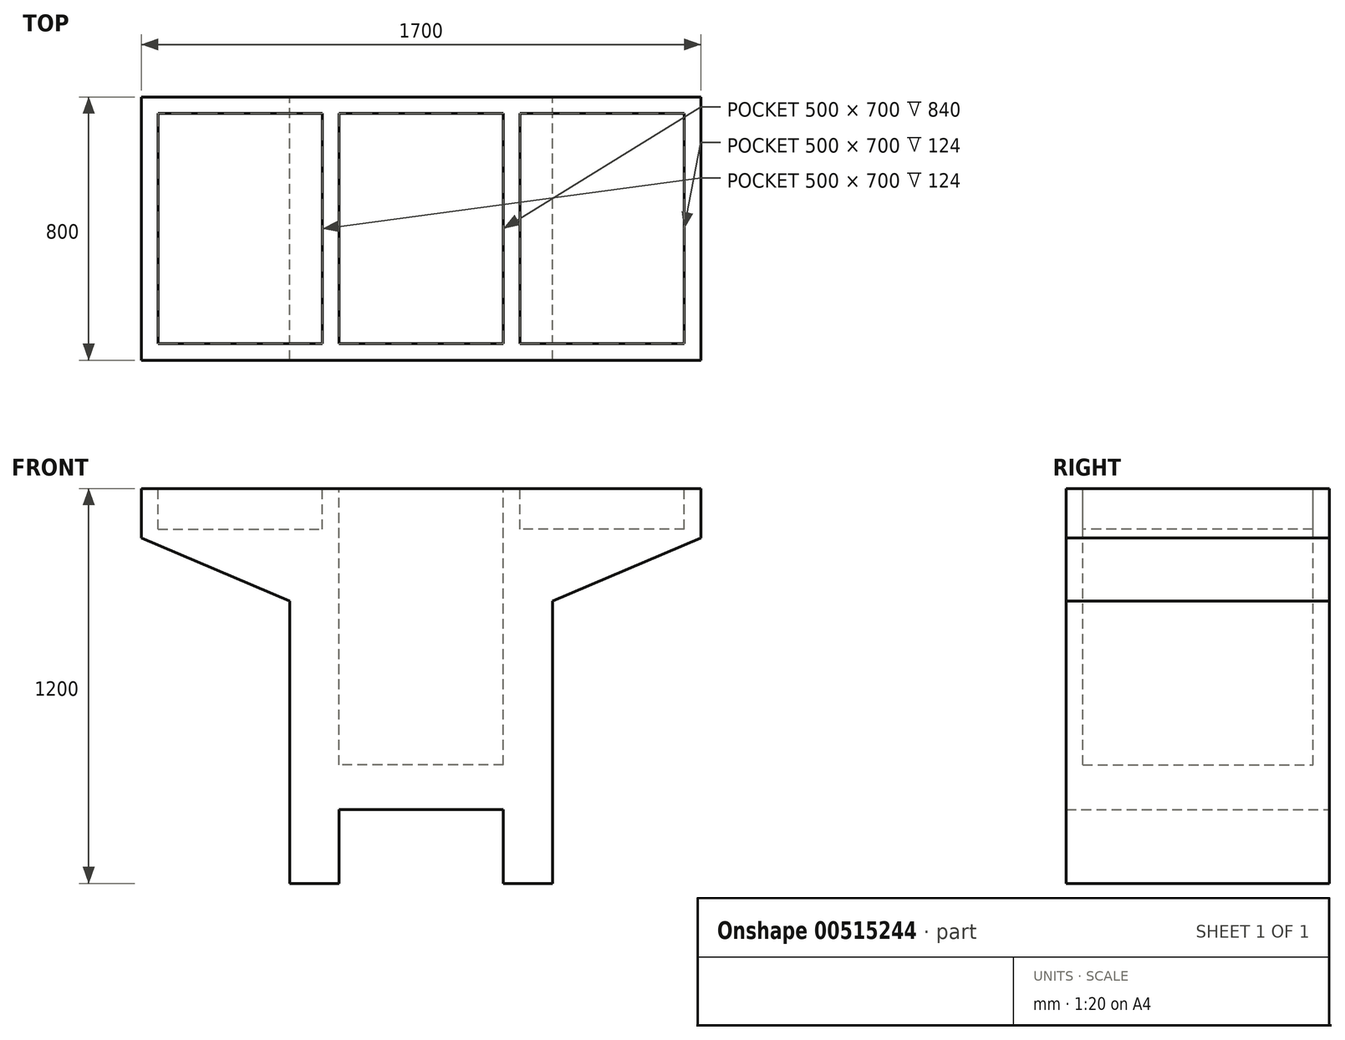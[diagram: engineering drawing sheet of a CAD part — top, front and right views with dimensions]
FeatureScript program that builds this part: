
annotation { "Feature Type Name" : "Feature", "Feature Type Description" : "" }
export const myFeature = defineFeature(function(context is Context, id is Id, definition is map)
    precondition{}
    {
        {
            var Q0;
            Q0=qCreatedBy(makeId("Front.planeOp"),FACE);
            var sketch = newSketch(context, id + "F0", { "sketchPlane" : qUnion([Q0])});
            skLineSegment(sketch, "E0", {"start": v(0, 224.9) * mm, "end": v(-250, 224.9) * mm});
            skLineSegment(sketch, "E1", {"start": v(-250, 224.9) * mm, "end": v(-250, 0) * mm});
            skLineSegment(sketch, "E2", {"start": v(-250, 0) * mm, "end": v(-400, 0) * mm});
            skLineSegment(sketch, "E3", {"start": v(-400, 0) * mm, "end": v(-400, 858.13) * mm});
            skLineSegment(sketch, "E4", {"start": v(-400, 858.13) * mm, "end": v(-850, 1050) * mm});
            skLineSegment(sketch, "E5", {"start": v(-850, 1050) * mm, "end": v(-850, 1200) * mm});
            skLineSegment(sketch, "E6", {"start": v(-850, 1200) * mm, "end": v(0, 1200) * mm});
            skLineSegment(sketch, "E7.MirrorCS", {"start": v(850, 1200) * mm, "end": v(0, 1200) * mm});
            skLineSegment(sketch, "E8.MirrorCS", {"start": v(850, 1050) * mm, "end": v(850, 1200) * mm});
            skLineSegment(sketch, "E9.MirrorCS", {"start": v(400, 858.13) * mm, "end": v(850, 1050) * mm});
            skLineSegment(sketch, "E10.MirrorCS", {"start": v(400, 0) * mm, "end": v(400, 858.13) * mm});
            skLineSegment(sketch, "E11.MirrorCS", {"start": v(250, 0) * mm, "end": v(400, 0) * mm});
            skLineSegment(sketch, "E12.MirrorCS", {"start": v(250, 224.9) * mm, "end": v(250, 0) * mm});
            skLineSegment(sketch, "E13.MirrorCS", {"start": v(0, 224.9) * mm, "end": v(250, 224.9) * mm});
            skSolve(sketch);
        }
        {
            var Q0;
            Q0 = qSketchRegion(id + "F0", true);
            extrude(context, id + "F1", {"entities" : qUnion([Q0]), "endBound" : BoundingType.SYMMETRIC, "depth" : 800 * mm, "offsetDistance" : 25 * mm});
        }
        {
            var Q0;
            Q0=makeQuery(id+"F1.opExtrude","SWEPT_FACE",FACE,{"disambiguationData":[OSD([sQuery(id+"F0.wireOp",EDGE,"E6"),sQuery(id+"F0.wireOp",EDGE,"E7.MirrorCS")])]});
            var sketch = newSketch(context, id + "F2", { "sketchPlane" : qUnion([Q0])});
            skLineSegment(sketch, "E14.bottom", {"start": v(250, -350) * mm, "end": v(-250, -350) * mm});
            skLineSegment(sketch, "E14.top", {"start": v(250, 350) * mm, "end": v(-250, 350) * mm});
            skLineSegment(sketch, "E14.left", {"start": v(250, -350) * mm, "end": v(250, 350) * mm});
            skLineSegment(sketch, "E14.right", {"start": v(-250, -350) * mm, "end": v(-250, 350) * mm});
            skPoint(sketch, "E14.middle", {"position": v(0, 0) * mm});
            skSolve(sketch);
        }
        {
            var Q0;
            Q0=makeQuery(id+"F2.imprint","IMPRINT",FACE,{"disambiguationData":[TD([[makeQuery(id+"F2.imprint","IMPRINT",EDGE,{"derivedFrom":sQuery(id+"F2.wireOp",EDGE,"E14.bottom")}),-1.0]])]});
            extrude(context, id + "F3", {"entities" : qUnion([Q0]), "operationType" : NewBodyOperationType.REMOVE, "oppositeDirection" : true, "depth" : 840 * mm, "offsetDistance" : 25 * mm});
        }
        {
            var Q0;
            Q0=makeQuery(id+"F1.opExtrude","SWEPT_FACE",FACE,{"disambiguationData":[OSD([sQuery(id+"F0.wireOp",EDGE,"E6"),sQuery(id+"F0.wireOp",EDGE,"E7.MirrorCS")])]});
            var sketch = newSketch(context, id + "F4", { "sketchPlane" : qUnion([Q0])});
            skLineSegment(sketch, "E15.bottom", {"start": v(-800, 350) * mm, "end": v(-300, 350) * mm});
            skLineSegment(sketch, "E15.top", {"start": v(-800, -350) * mm, "end": v(-300, -350) * mm});
            skLineSegment(sketch, "E15.left", {"start": v(-800, 350) * mm, "end": v(-800, -350) * mm});
            skLineSegment(sketch, "E15.right", {"start": v(-300, 350) * mm, "end": v(-300, -350) * mm});
            skLineSegment(sketch, "E16.MirrorCS", {"start": v(800, -350) * mm, "end": v(300, -350) * mm});
            skLineSegment(sketch, "E17.MirrorCS", {"start": v(800, 350) * mm, "end": v(800, -350) * mm});
            skLineSegment(sketch, "E18.MirrorCS", {"start": v(300, 350) * mm, "end": v(300, -350) * mm});
            skLineSegment(sketch, "E19.MirrorCS", {"start": v(800, 350) * mm, "end": v(300, 350) * mm});
            skSolve(sketch);
        }
        {
            var Q0;
            Q0=makeQuery(id+"F4.imprint","IMPRINT",FACE,{"disambiguationData":[TD([[makeQuery(id+"F4.imprint","IMPRINT",EDGE,{"derivedFrom":sQuery(id+"F4.wireOp",EDGE,"E15.bottom")}),-1.0]])]});
            var Q1;
            Q1=makeQuery(id+"F4.imprint","IMPRINT",FACE,{"disambiguationData":[TD([[makeQuery(id+"F4.imprint","IMPRINT",EDGE,{"derivedFrom":sQuery(id+"F4.wireOp",EDGE,"E16.MirrorCS")}),-1.0]])]});
            extrude(context, id + "F5", {"entities" : qUnion([Q0, Q1]), "operationType" : NewBodyOperationType.REMOVE, "oppositeDirection" : true, "depth" : 124 * mm, "offsetDistance" : 25 * mm});
        }
    });
